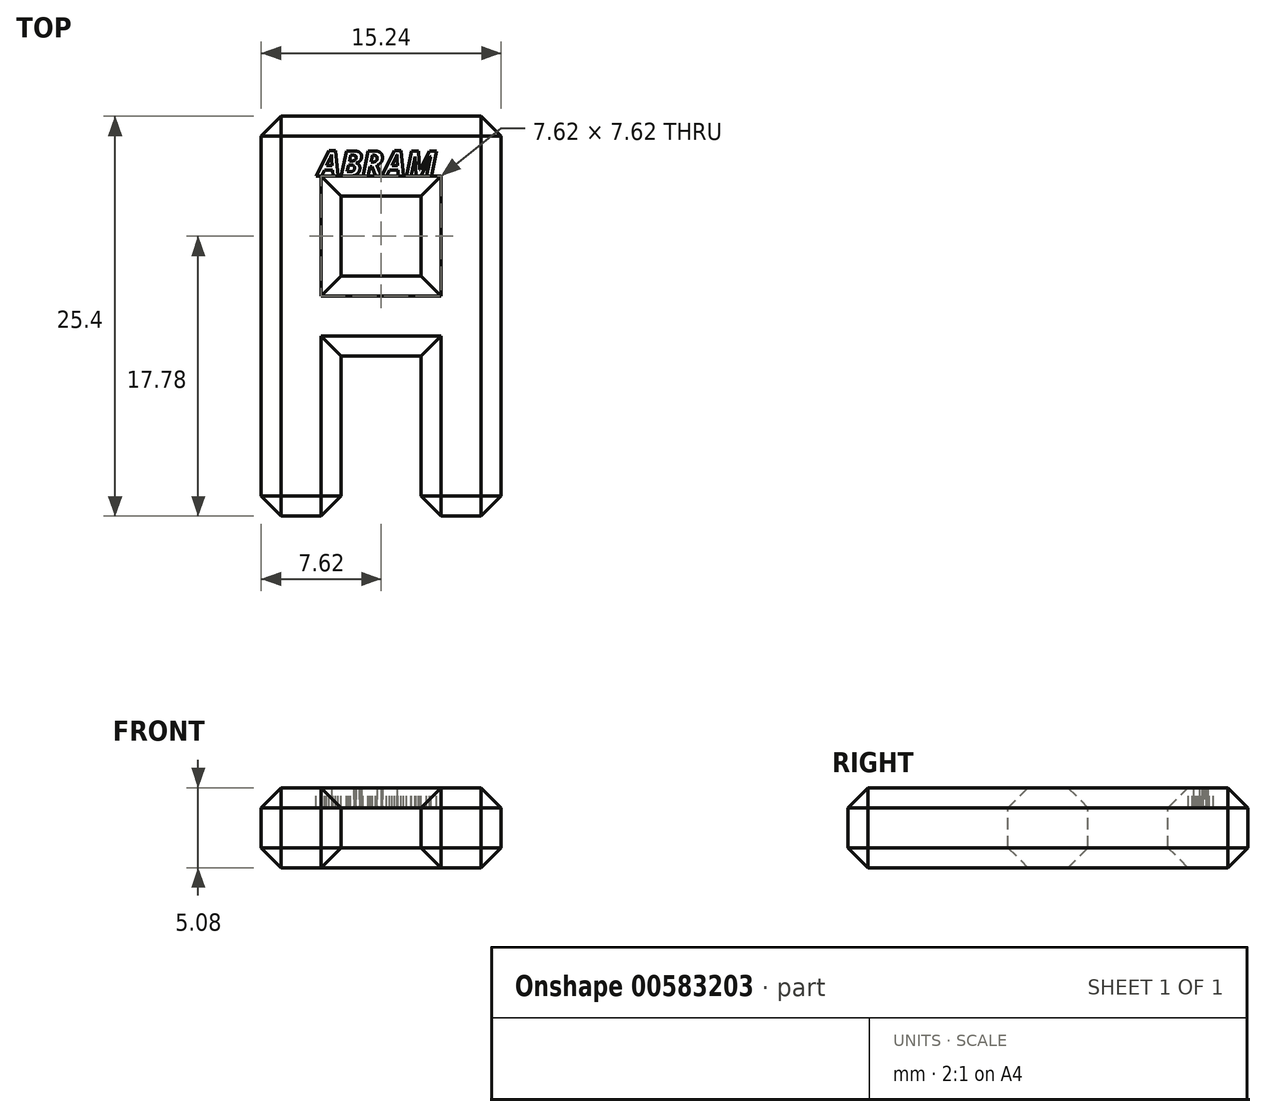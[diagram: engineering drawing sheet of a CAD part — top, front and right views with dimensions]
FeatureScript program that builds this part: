
annotation { "Feature Type Name" : "Feature", "Feature Type Description" : "" }
export const myFeature = defineFeature(function(context is Context, id is Id, definition is map)
    precondition{}
    {
        {
            var Q0;
            Q0=qCreatedBy(makeId("Top.planeOp"),FACE);
            var sketch = newSketch(context, id + "F0", { "sketchPlane" : qUnion([Q0])});
            skLineSegment(sketch, "E0.bottom", {"start": v(7.62, 12.7) * mm, "end": v(-7.62, 12.7) * mm});
            skLineSegment(sketch, "E0.top", {"start": v(7.62, -12.7) * mm, "end": v(-7.62, -12.7) * mm});
            skLineSegment(sketch, "E0.left", {"start": v(7.62, 12.7) * mm, "end": v(7.62, -12.7) * mm});
            skLineSegment(sketch, "E0.right", {"start": v(-7.62, 12.7) * mm, "end": v(-7.62, -12.7) * mm});
            skPoint(sketch, "E0.middle", {"position": v(0, 0) * mm});
            skSolve(sketch);
        }
        {
            var Q0;
            Q0=makeQuery(id+"F0.imprint","IMPRINT",FACE,{"disambiguationData":[TD([[makeQuery(id+"F0.imprint","IMPRINT",EDGE,{"derivedFrom":sQuery(id+"F0.wireOp",EDGE,"E0.bottom")}),1.0]])]});
            extrude(context, id + "F1", {"entities" : qUnion([Q0]), "depth" : 5.08 * mm, "offsetDistance" : 25.4 * mm});
        }
        {
            var Q0;
            Q0=makeQuery(id+"F1.opExtrude","CAP_FACE",FACE,{"disambiguationData":[OSD([sQuery(id+"F0.wireOp",EDGE,"E0.bottom"),sQuery(id+"F0.wireOp",EDGE,"E0.top"),sQuery(id+"F0.wireOp",EDGE,"E0.left"),sQuery(id+"F0.wireOp",EDGE,"E0.right")])],"isStart":false});
            var sketch = newSketch(context, id + "F2", { "sketchPlane" : qUnion([Q0])});
            skLineSegment(sketch, "E1.bottom", {"start": v(-2.54, -12.7) * mm, "end": v(2.54, -12.7) * mm});
            skLineSegment(sketch, "E1.top", {"start": v(-2.54, -2.54) * mm, "end": v(2.54, -2.54) * mm});
            skLineSegment(sketch, "E1.left", {"start": v(-2.54, -12.7) * mm, "end": v(-2.54, -2.54) * mm});
            skLineSegment(sketch, "E1.right", {"start": v(2.54, -12.7) * mm, "end": v(2.54, -2.54) * mm});
            skLineSegment(sketch, "E2.bottom", {"start": v(-2.54, 7.62) * mm, "end": v(2.54, 7.62) * mm});
            skLineSegment(sketch, "E2.top", {"start": v(-2.54, 2.54) * mm, "end": v(2.54, 2.54) * mm});
            skLineSegment(sketch, "E2.left", {"start": v(-2.54, 7.62) * mm, "end": v(-2.54, 2.54) * mm});
            skLineSegment(sketch, "E2.right", {"start": v(2.54, 7.62) * mm, "end": v(2.54, 2.54) * mm});
            skSolve(sketch);
        }
        {
            var Q0;
            Q0=makeQuery(id+"F2.imprint","IMPRINT",FACE,{"disambiguationData":[TD([[makeQuery(id+"F2.imprint","IMPRINT",EDGE,{"derivedFrom":sQuery(id+"F2.wireOp",EDGE,"E2.bottom")}),-1.0]])]});
            var Q1;
            Q1=makeQuery(id+"F2.imprint","IMPRINT",FACE,{"disambiguationData":[TD([[makeQuery(id+"F2.imprint","IMPRINT",EDGE,{"derivedFrom":sQuery(id+"F2.wireOp",EDGE,"E1.bottom")}),-1.0]])]});
            extrude(context, id + "F3", {"entities" : qUnion([Q0, Q1]), "operationType" : NewBodyOperationType.REMOVE, "oppositeDirection" : true, "depth" : 5.08 * mm, "offsetDistance" : 25.4 * mm});
        }
        {
            var Q0;
            Q0=makeQuery(id+"F1.opExtrude","SWEPT_EDGE",EDGE,{"disambiguationData":[OSD([sQuery(id+"F0.wireOp",EDGE,"E0.bottom"),sQuery(id+"F0.wireOp",EDGE,"E0.right")])]});
            var Q1;
            Q1=makeQuery(id+"F1.opExtrude","SWEPT_FACE",FACE,{"disambiguationData":[OSD([sQuery(id+"F0.wireOp",EDGE,"E0.bottom")])]});
            var Q2;
            Q2=makeQuery(id+"F1.opExtrude","SWEPT_FACE",FACE,{"disambiguationData":[OSD([sQuery(id+"F0.wireOp",EDGE,"E0.right")])]});
            var Q3;
            Q3=makeQuery(id+"F1.opExtrude","SWEPT_FACE",FACE,{"disambiguationData":[OSD([sQuery(id+"F0.wireOp",EDGE,"E0.left")])]});
            var Q4;
            Q4=makeQuery(id+"F1.opExtrude","CAP_FACE",FACE,{"disambiguationData":[OSD([sQuery(id+"F0.wireOp",EDGE,"E0.bottom"),sQuery(id+"F0.wireOp",EDGE,"E0.top"),sQuery(id+"F0.wireOp",EDGE,"E0.left"),sQuery(id+"F0.wireOp",EDGE,"E0.right")])],"isStart":false});
            var Q5;
            {var subQ0=sQuery(id+"F0.wireOp",EDGE,"E0.right");var subQ2=sQuery(id+"F0.wireOp",EDGE,"E0.top");Q5=makeQuery(id+"F3.boolean.opBoolean","SPLIT",FACE,{"disambiguationData":[TD([makeQuery(id+"F1.opExtrude","SWEPT_FACE",FACE,{"disambiguationData":[OSD([subQ0])]})])],"derivedFrom":makeQuery(id+"F1.opExtrude","SWEPT_FACE",FACE,{"disambiguationData":[OSD([subQ2])]})});}
            var Q6;
            {var subQ1=sQuery(id+"F0.wireOp",EDGE,"E0.left");var subQ2=sQuery(id+"F0.wireOp",EDGE,"E0.top");Q6=makeQuery(id+"F3.boolean.opBoolean","SPLIT",FACE,{"disambiguationData":[TD([makeQuery(id+"F1.opExtrude","SWEPT_FACE",FACE,{"disambiguationData":[OSD([subQ1])]})])],"derivedFrom":makeQuery(id+"F1.opExtrude","SWEPT_FACE",FACE,{"disambiguationData":[OSD([subQ2])]})});}
            var Q7;
            Q7=makeQuery(id+"F1.opExtrude","CAP_FACE",FACE,{"disambiguationData":[OSD([sQuery(id+"F0.wireOp",EDGE,"E0.bottom"),sQuery(id+"F0.wireOp",EDGE,"E0.top"),sQuery(id+"F0.wireOp",EDGE,"E0.left"),sQuery(id+"F0.wireOp",EDGE,"E0.right")])],"isStart":true});
            chamfer(context, id + "F4", {"entities" : qUnion([Q0, Q1, Q2, Q3, Q4, Q5, Q6, Q7]), "width" : 1.27 * mm, "tangentPropagation" : true});
        }
        {
            var Q0;
            Q0=makeQuery(id+"F1.opExtrude","CAP_FACE",FACE,{"disambiguationData":[OSD([sQuery(id+"F0.wireOp",EDGE,"E0.bottom"),sQuery(id+"F0.wireOp",EDGE,"E0.top"),sQuery(id+"F0.wireOp",EDGE,"E0.left"),sQuery(id+"F0.wireOp",EDGE,"E0.right")])],"isStart":false});
            var sketch = newSketch(context, id + "F5", { "sketchPlane" : qUnion([Q0])});
            skText(sketch, "E3", { "text": "ABRAM", "fontName": "OpenSans-BoldItalic.ttf"});
            const initialGuessF5  = {"E3": [-0.00402, 0.0089, 1, 0, 0.00161]};
            skSetInitialGuess(sketch, initialGuessF5);
            skSolve(sketch);
        }
        {
            var Q0;
            Q0 = qSketchRegion(id + "F5", true);
            extrude(context, id + "F6", {"entities" : qUnion([Q0]), "operationType" : NewBodyOperationType.REMOVE, "oppositeDirection" : true, "depth" : 1.27 * mm, "offsetDistance" : 25.4 * mm});
        }
    });
